# Revit family: FU-Chair_Sandler_Timber 5-2
name_source: partatom
category: Furniture
units: mm (PartAtom-declared; Revit-internal decimal feet)

## family parameters
Always vertical = Yes
Cut with Voids When Loaded = No
OmniClass Number = 23.40.20.00
OmniClass Title = General Furniture and Specialties
Room Calculation Point = No
Shared = No
Work Plane-Based = No

## types (1)
- Timber 5.2
    Default Elevation = 0 mm  [stored 0 ft]
    Depth = 625 mm  [stored 2.05052 ft]
    Description = Lounge chair with upholstered seat, wooden back and upholstered back panel on a solid beech frame.
    Height = 765 mm  [stored 2.50984 ft]
    Manufacturer = Sandler
    Model = Timber 5.2
    URL = https://www.sandlerseating.com
    Width = 575 mm  [stored 1.88648 ft]

note: [stored X ft] marks values corroborated as IEEE doubles in the binary element streams (Revit-internal decimal feet)

## geometry (parser evidence)
native form markers: Sweep x3
no freeform markers — native parametric forms only
